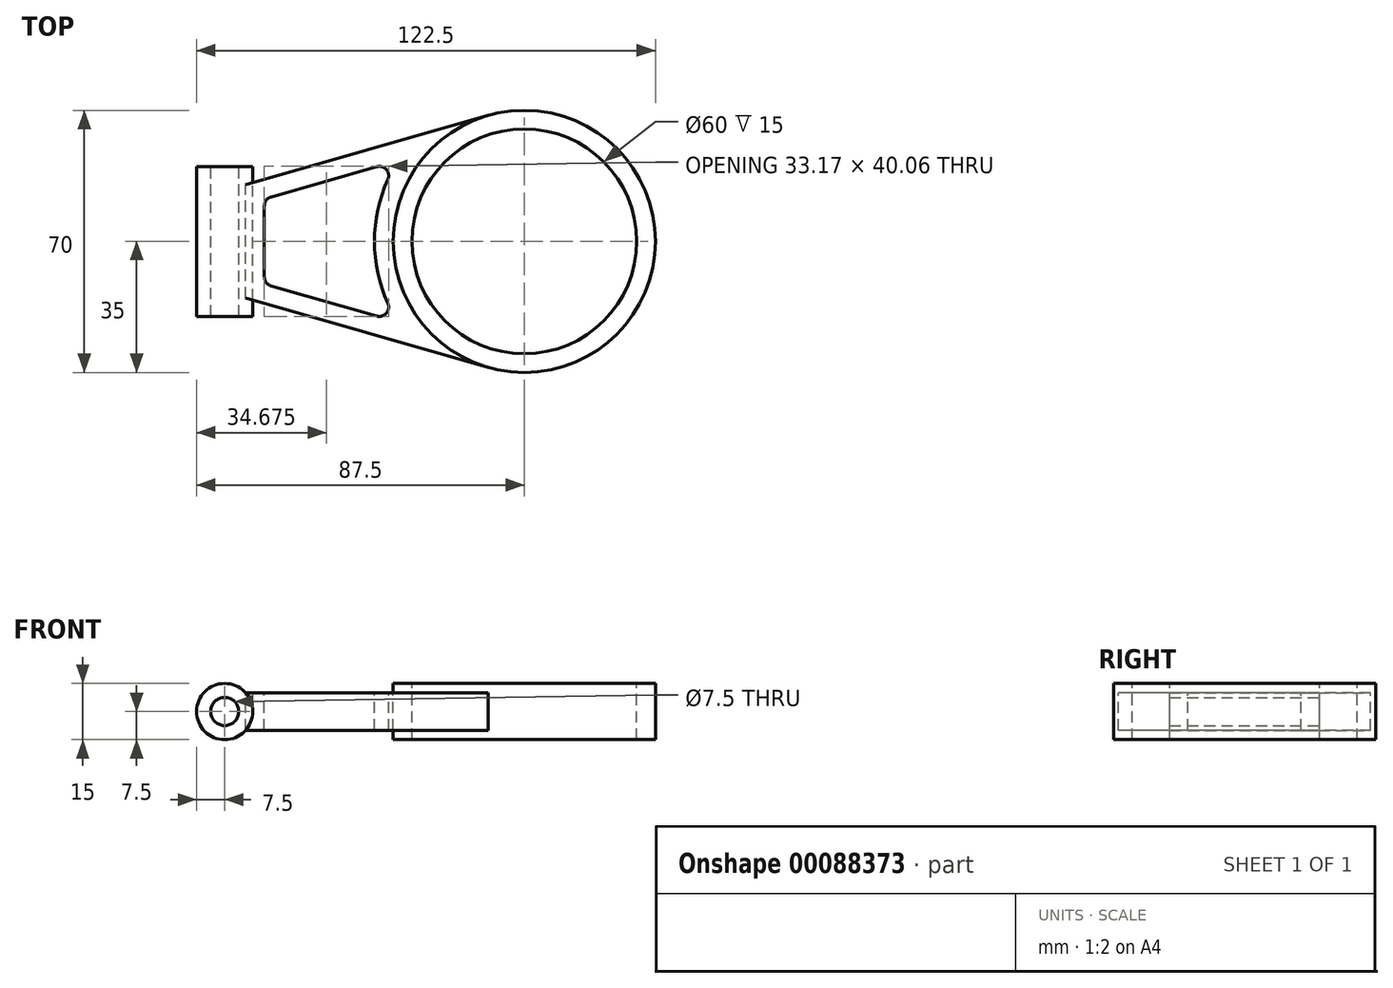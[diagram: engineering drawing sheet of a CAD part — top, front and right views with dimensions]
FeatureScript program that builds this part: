
annotation { "Feature Type Name" : "Feature", "Feature Type Description" : "" }
export const myFeature = defineFeature(function(context is Context, id is Id, definition is map)
    precondition{}
    {
        {
            var Q0;
            Q0=qCreatedBy(makeId("Top.planeOp"),FACE);
            var sketch = newSketch(context, id + "F0", { "sketchPlane" : qUnion([Q0])});
            skLineSegment(sketch, "E0", {"start": v(0, 0) * mm, "end": v(-80, 0) * mm, "construction": true});
            skArc(sketch, "E1.0", {"start": v(-9.62, 33.65) * mm, "mid": v(-35, 0) * mm, "end": v(-9.62, -33.65) * mm});
            skArc(sketch, "E2.0", {"start": v(-36.44, 16.5) * mm, "mid": v(-40, 0) * mm, "end": v(-36.44, -16.5) * mm});
            skLineSegment(sketch, "E3", {"start": v(-87.5, 20) * mm, "end": v(-87.5, -20) * mm, "construction": true});
            skLineSegment(sketch, "E4", {"start": v(-87.5, 20) * mm, "end": v(-72.5, 20) * mm, "construction": true});
            skLineSegment(sketch, "E5", {"start": v(-87.5, -20) * mm, "end": v(-72.5, -20) * mm, "construction": true});
            skLineSegment(sketch, "E6", {"start": v(-72.5, 20) * mm, "end": v(-72.5, -20) * mm, "construction": true});
            skLineSegment(sketch, "E7", {"start": v(-80, 20) * mm, "end": v(-80, -20) * mm, "construction": true});
            skPoint(sketch, "E8", {"position": v(-80, 0) * mm});
            skLineSegment(sketch, "E9", {"start": v(-74.41, -15.13) * mm, "end": v(-74.41, 15.12) * mm});
            skPoint(sketch, "E10", {"position": v(-74.41, 0) * mm});
            skLineSegment(sketch, "E11", {"start": v(0, 0) * mm, "end": v(-74.41, 0) * mm, "construction": true});
            skLineSegment(sketch, "E12", {"start": v(-74.41, -15.13) * mm, "end": v(-9.62, -33.65) * mm});
            skLineSegment(sketch, "E13.MirrorCS", {"start": v(-74.41, 15.13) * mm, "end": v(-9.62, 33.65) * mm});
            skPoint(sketch, "E14.orphan", {"position": v(30.23, 45.05) * mm});
            skLineSegment(sketch, "E15.0", {"start": v(-67.6, 11.87) * mm, "end": v(-39.4, 19.93) * mm});
            skLineSegment(sketch, "E16.trimOffspring", {"start": v(-69.4, 9.47) * mm, "end": v(-69.4, -9.47) * mm});
            skLineSegment(sketch, "E17.MirrorCS", {"start": v(-67.6, -11.87) * mm, "end": v(-39.4, -19.93) * mm});
            skPoint(sketch, "E18.visualSharp", {"position": v(-69.41, 11.35) * mm});
            skArc(sketch, "E18.filletArc", {"start": v(-67.6, 11.87) * mm, "mid": v(-68.9, 10.97) * mm, "end": v(-69.41, 9.47) * mm});
            skPoint(sketch, "E19.visualSharp", {"position": v(-69.4, -11.35) * mm});
            skArc(sketch, "E19.filletArc", {"start": v(-69.41, -9.47) * mm, "mid": v(-68.9, -10.97) * mm, "end": v(-67.6, -11.87) * mm});
            skArc(sketch, "E20", {"start": v(-36.44, 16.5) * mm, "mid": v(-36.82, 19.16) * mm, "end": v(-39.4, 19.93) * mm});
            skArc(sketch, "E21.MirrorCS", {"start": v(-36.44, -16.5) * mm, "mid": v(-36.82, -19.16) * mm, "end": v(-39.4, -19.93) * mm});
            skSolve(sketch);
        }
        {
            var Q0;
            Q0=qCreatedBy(makeId("Top.planeOp"),FACE);
            cPlane(context, id + "F1", {"entities" : qUnion([Q0]), "cplaneType" : CPlaneType.OFFSET, "offset" : 2.5 * mm, "width" : 150 * mm, "height" : 150 * mm});
        }
        {
            var Q0;
            Q0=qCreatedBy(id+"F1.planeOp",FACE);
            var sketch = newSketch(context, id + "F2", { "sketchPlane" : qUnion([Q0])});
            skCircle(sketch, "E22.0", {"center": v(0, 0) * mm, "radius": 35 * mm});
            skCircle(sketch, "E23.0", {"center": v(0, 0) * mm, "radius": 30 * mm});
            skSolve(sketch);
        }
        {
            var Q0;
            Q0 = qSketchRegion(id + "F2", true);
            extrude(context, id + "F3", {"entities" : qUnion([Q0]), "oppositeDirection" : true, "depth" : 15 * mm});
        }
        {
            var Q0;
            Q0=qCreatedBy(makeId("Front.planeOp"),FACE);
            var sketch = newSketch(context, id + "F4", { "sketchPlane" : qUnion([Q0])});
            skLineSegment(sketch, "E24", {"start": v(-80, 0) * mm, "end": v(-80, -5) * mm, "construction": true});
            skCircle(sketch, "E25", {"center": v(-80, -5) * mm, "radius": 3.75 * mm});
            skCircle(sketch, "E26", {"center": v(-80, -5) * mm, "radius": 7.5 * mm});
            skSolve(sketch);
        }
        {
            var Q0;
            Q0 = qSketchRegion(id + "F4", true);
            extrude(context, id + "F5", {"entities" : qUnion([Q0]), "endBound" : BoundingType.SYMMETRIC, "depth" : 40 * mm});
        }
        {
            var Q0;
            Q0 = qSketchRegion(id + "F0", true);
            extrude(context, id + "F6", {"entities" : qUnion([Q0]), "oppositeDirection" : true, "depth" : 10 * mm});
        }
    });
